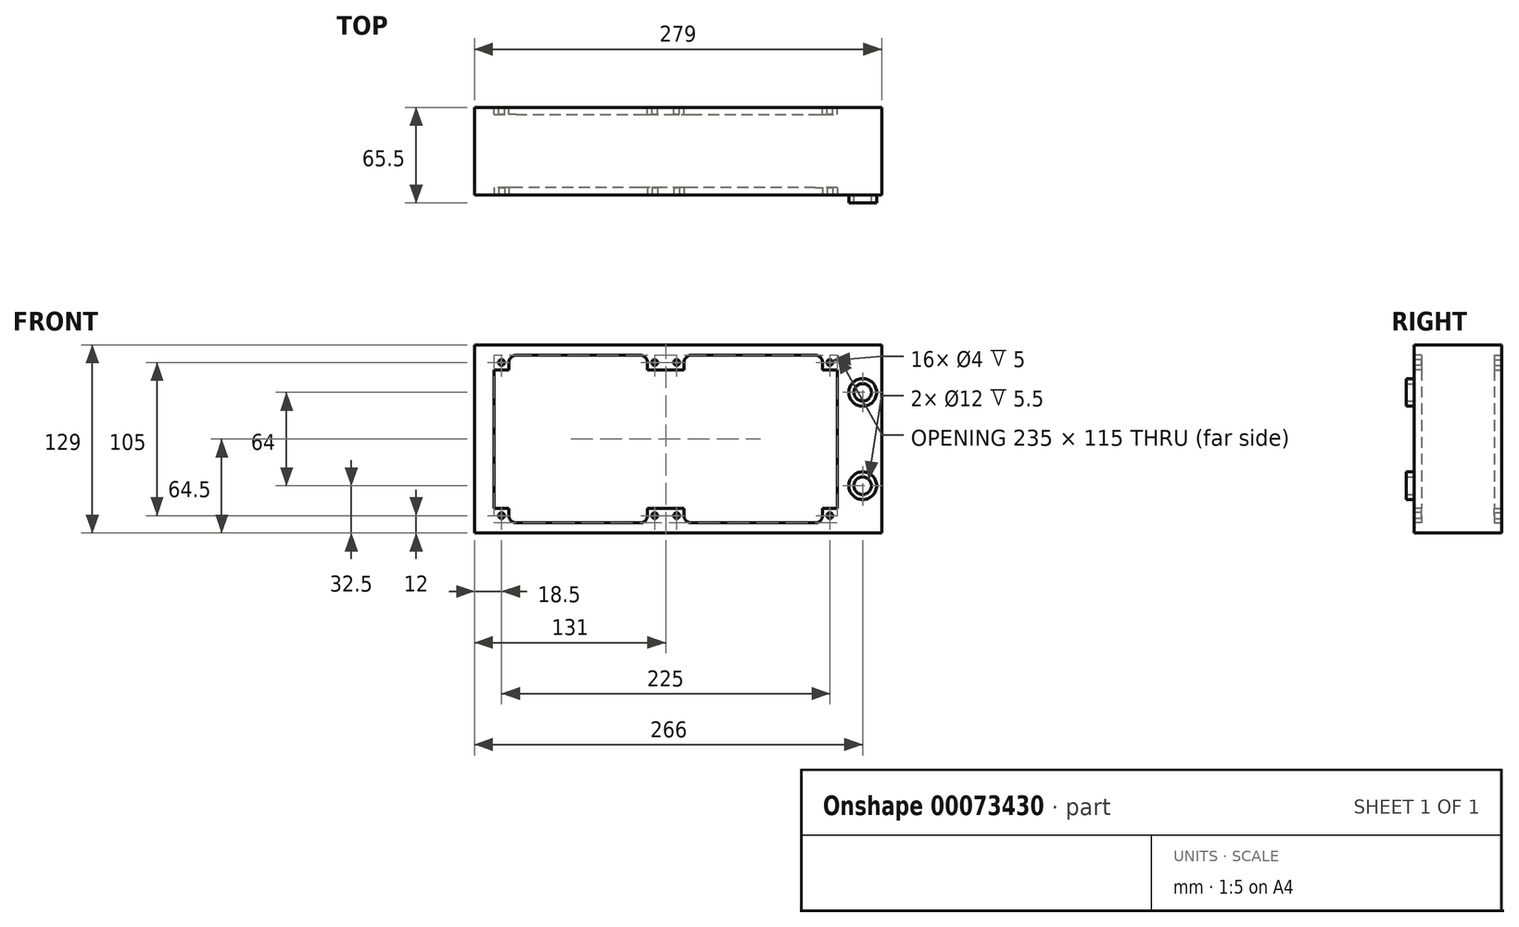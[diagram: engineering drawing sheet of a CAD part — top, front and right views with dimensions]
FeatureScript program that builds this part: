
annotation { "Feature Type Name" : "Feature", "Feature Type Description" : "" }
export const myFeature = defineFeature(function(context is Context, id is Id, definition is map)
    precondition{}
    {
        {
            var Q0;
            Q0=qCreatedBy(makeId("Front.planeOp"),FACE);
            var sketch = newSketch(context, id + "F0", { "sketchPlane" : qUnion([Q0])});
            skLineSegment(sketch, "E0.bottom", {"start": v(0, 64.5) * mm, "end": v(279, 64.5) * mm});
            skLineSegment(sketch, "E0.top", {"start": v(0, -64.5) * mm, "end": v(279, -64.5) * mm});
            skLineSegment(sketch, "E0.left", {"start": v(0, 64.5) * mm, "end": v(0, -64.5) * mm});
            skLineSegment(sketch, "E0.right", {"start": v(279, 64.5) * mm, "end": v(279, -64.5) * mm});
            skSolve(sketch);
        }
        {
            var Q0;
            Q0=qSketchRegion(id+"F0",true);
            extrude(context, id + "F1", {"entities" : qUnion([Q0]), "depth" : 60 * mm});
        }
        {
            var Q0;
            Q0=makeQuery(id+"F1.opExtrude","CAP_FACE",FACE,{"disambiguationData":[OSD([sQuery(id+"F0.wireOp",EDGE,"E0.bottom"),sQuery(id+"F0.wireOp",EDGE,"E0.top"),sQuery(id+"F0.wireOp",EDGE,"E0.left"),sQuery(id+"F0.wireOp",EDGE,"E0.right")])],"isStart":false});
            var sketch = newSketch(context, id + "F2", { "sketchPlane" : qUnion([Q0])});
            skCircle(sketch, "E1", {"center": v(266, -32) * mm, "radius": 9.5 * mm});
            skCircle(sketch, "E2", {"center": v(266, 32) * mm, "radius": 9.5 * mm});
            skLineSegment(sketch, "E3", {"start": v(0, 0) * mm, "end": v(279, 0) * mm, "construction": true});
            skCircle(sketch, "E4", {"center": v(266, 32) * mm, "radius": 6 * mm});
            skCircle(sketch, "E5", {"center": v(266, -32) * mm, "radius": 6 * mm});
            skSolve(sketch);
        }
        {
            var Q0;
            Q0=qSketchRegion(id+"F2",true);
            extrude(context, id + "F3", {"entities" : qUnion([Q0]), "operationType" : NewBodyOperationType.ADD, "depth" : 5.5 * mm});
        }
        {
            var Q0;
            {var subQ0=sQuery(id+"F0.wireOp",EDGE,"E0.right");var subQ1=sQuery(id+"F0.wireOp",EDGE,"E0.left");var subQ2=sQuery(id+"F0.wireOp",EDGE,"E0.top");var subQ3=sQuery(id+"F0.wireOp",EDGE,"E0.bottom");Q0=makeQuery(id+"F3.boolean.opBoolean","SPLIT",FACE,{"disambiguationData":[TD([makeQuery(id+"F1.opExtrude","SWEPT_FACE",FACE,{"disambiguationData":[OSD([subQ3])]})])],"derivedFrom":makeQuery(id+"F1.opExtrude","CAP_FACE",FACE,{"disambiguationData":[OSD([subQ3,subQ2,subQ1,subQ0])],"isStart":false})});}
            var sketch = newSketch(context, id + "F4", { "sketchPlane" : qUnion([Q0])});
            skCircle(sketch, "E6", {"center": v(18.5, 52.5) * mm, "radius": 2 * mm});
            skCircle(sketch, "E7", {"center": v(123.5, 52.5) * mm, "radius": 2 * mm});
            skCircle(sketch, "E8", {"center": v(138.5, 52.5) * mm, "radius": 2 * mm});
            skCircle(sketch, "E9", {"center": v(243.5, 52.5) * mm, "radius": 2 * mm});
            skLineSegment(sketch, "E10", {"start": v(13.5, 47.5) * mm, "end": v(13.5, 0) * mm});
            skLineSegment(sketch, "E11", {"start": v(248.5, 0) * mm, "end": v(248.5, 47.5) * mm});
            skLineSegment(sketch, "E12", {"start": v(248.5, 47.5) * mm, "end": v(238.5, 47.5) * mm});
            skLineSegment(sketch, "E13", {"start": v(238.5, 47.5) * mm, "end": v(238.5, 52.5) * mm});
            skLineSegment(sketch, "E14", {"start": v(233.5, 57.5) * mm, "end": v(148.5, 57.5) * mm});
            skLineSegment(sketch, "E15", {"start": v(143.5, 52.5) * mm, "end": v(143.5, 47.5) * mm});
            skLineSegment(sketch, "E16", {"start": v(143.5, 47.5) * mm, "end": v(118.5, 47.5) * mm});
            skLineSegment(sketch, "E17", {"start": v(118.5, 47.5) * mm, "end": v(118.5, 52.5) * mm});
            skLineSegment(sketch, "E18", {"start": v(113.5, 57.5) * mm, "end": v(28.5, 57.5) * mm});
            skLineSegment(sketch, "E19", {"start": v(23.5, 52.5) * mm, "end": v(23.5, 47.5) * mm});
            skLineSegment(sketch, "E20", {"start": v(23.5, 47.5) * mm, "end": v(13.5, 47.5) * mm});
            skLineSegment(sketch, "E21", {"start": v(0, 0) * mm, "end": v(279, 0) * mm, "construction": true});
            skPoint(sketch, "E22.visualSharp", {"position": v(143.5, 57.5) * mm});
            skArc(sketch, "E22.filletArc", {"start": v(148.5, 57.5) * mm, "mid": v(144.96, 56.04) * mm, "end": v(143.5, 52.5) * mm});
            skPoint(sketch, "E23.visualSharp", {"position": v(118.5, 57.5) * mm});
            skArc(sketch, "E23.filletArc", {"start": v(118.5, 52.5) * mm, "mid": v(117.04, 56.04) * mm, "end": v(113.5, 57.5) * mm});
            skPoint(sketch, "E24.visualSharp", {"position": v(238.5, 57.5) * mm});
            skArc(sketch, "E24.filletArc", {"start": v(238.5, 52.5) * mm, "mid": v(237.04, 56.04) * mm, "end": v(233.5, 57.5) * mm});
            skPoint(sketch, "E25.visualSharp", {"position": v(23.5, 57.5) * mm});
            skArc(sketch, "E25.filletArc", {"start": v(28.5, 57.5) * mm, "mid": v(24.96, 56.04) * mm, "end": v(23.5, 52.5) * mm});
            skCircle(sketch, "E26.MirrorC", {"center": v(243.5, -52.5) * mm, "radius": 2 * mm});
            skLineSegment(sketch, "E27.MirrorCS", {"start": v(248.5, 0) * mm, "end": v(248.5, -47.5) * mm});
            skLineSegment(sketch, "E28.MirrorCS", {"start": v(248.5, -47.5) * mm, "end": v(238.5, -47.5) * mm});
            skLineSegment(sketch, "E29.MirrorCS", {"start": v(238.5, -47.5) * mm, "end": v(238.5, -52.5) * mm});
            skArc(sketch, "E30.MirrorCS", {"start": v(238.5, -52.5) * mm, "mid": v(237.04, -56.04) * mm, "end": v(233.5, -57.5) * mm});
            skLineSegment(sketch, "E31.MirrorCS", {"start": v(233.5, -57.5) * mm, "end": v(148.5, -57.5) * mm});
            skArc(sketch, "E32.MirrorCS", {"start": v(148.5, -57.5) * mm, "mid": v(144.96, -56.04) * mm, "end": v(143.5, -52.5) * mm});
            skLineSegment(sketch, "E33.MirrorCS", {"start": v(143.5, -52.5) * mm, "end": v(143.5, -47.5) * mm});
            skCircle(sketch, "E34.MirrorC", {"center": v(138.5, -52.5) * mm, "radius": 2 * mm});
            skCircle(sketch, "E35.MirrorC", {"center": v(123.5, -52.5) * mm, "radius": 2 * mm});
            skLineSegment(sketch, "E36.MirrorCS", {"start": v(143.5, -47.5) * mm, "end": v(118.5, -47.5) * mm});
            skCircle(sketch, "E37.MirrorC", {"center": v(18.5, -52.5) * mm, "radius": 2 * mm});
            skLineSegment(sketch, "E38.MirrorCS", {"start": v(118.5, -47.5) * mm, "end": v(118.5, -52.5) * mm});
            skArc(sketch, "E39.MirrorCS", {"start": v(118.5, -52.5) * mm, "mid": v(117.04, -56.04) * mm, "end": v(113.5, -57.5) * mm});
            skLineSegment(sketch, "E40.MirrorCS", {"start": v(113.5, -57.5) * mm, "end": v(28.5, -57.5) * mm});
            skArc(sketch, "E41.MirrorCS", {"start": v(28.5, -57.5) * mm, "mid": v(24.96, -56.04) * mm, "end": v(23.5, -52.5) * mm});
            skLineSegment(sketch, "E42.MirrorCS", {"start": v(23.5, -52.5) * mm, "end": v(23.5, -47.5) * mm});
            skLineSegment(sketch, "E43.MirrorCS", {"start": v(13.5, -47.5) * mm, "end": v(13.5, 0) * mm});
            skLineSegment(sketch, "E44.MirrorCS", {"start": v(23.5, -47.5) * mm, "end": v(13.5, -47.5) * mm});
            skSolve(sketch);
        }
        {
            var Q0;
            Q0=qSketchRegion(id+"F4",true);
            extrude(context, id + "F5", {"entities" : qUnion([Q0]), "operationType" : NewBodyOperationType.REMOVE, "oppositeDirection" : true, "depth" : 5 * mm});
        }
        {
            var Q0;
            Q0=makeQuery(id+"F1.opExtrude","CAP_FACE",FACE,{"disambiguationData":[OSD([sQuery(id+"F0.wireOp",EDGE,"E0.bottom"),sQuery(id+"F0.wireOp",EDGE,"E0.top"),sQuery(id+"F0.wireOp",EDGE,"E0.left"),sQuery(id+"F0.wireOp",EDGE,"E0.right")])],"isStart":true});
            var sketch = newSketch(context, id + "F6", { "sketchPlane" : qUnion([Q0])});
            skCircle(sketch, "E45", {"center": v(-243.5, 52.5) * mm, "radius": 2 * mm});
            skCircle(sketch, "E46", {"center": v(-138.5, 52.5) * mm, "radius": 2 * mm});
            skCircle(sketch, "E47", {"center": v(-123.5, 52.5) * mm, "radius": 2 * mm});
            skCircle(sketch, "E48", {"center": v(-18.5, 52.5) * mm, "radius": 2 * mm});
            skLineSegment(sketch, "E49", {"start": v(-248.5, 47.5) * mm, "end": v(-248.5, 0) * mm});
            skLineSegment(sketch, "E50", {"start": v(-13.5, 0) * mm, "end": v(-13.5, 47.5) * mm});
            skLineSegment(sketch, "E51", {"start": v(-13.5, 47.5) * mm, "end": v(-23.5, 47.5) * mm});
            skLineSegment(sketch, "E52", {"start": v(-23.5, 47.5) * mm, "end": v(-23.5, 52.5) * mm});
            skLineSegment(sketch, "E53", {"start": v(-28.5, 57.5) * mm, "end": v(-113.5, 57.5) * mm});
            skLineSegment(sketch, "E54", {"start": v(-118.5, 52.5) * mm, "end": v(-118.5, 47.5) * mm});
            skLineSegment(sketch, "E55", {"start": v(-118.5, 47.5) * mm, "end": v(-143.5, 47.5) * mm});
            skLineSegment(sketch, "E56", {"start": v(-143.5, 47.5) * mm, "end": v(-143.5, 52.5) * mm});
            skLineSegment(sketch, "E57", {"start": v(-148.5, 57.5) * mm, "end": v(-233.5, 57.5) * mm});
            skLineSegment(sketch, "E58", {"start": v(-238.5, 52.5) * mm, "end": v(-238.5, 47.5) * mm});
            skLineSegment(sketch, "E59", {"start": v(-238.5, 47.5) * mm, "end": v(-248.5, 47.5) * mm});
            skLineSegment(sketch, "E60", {"start": v(-279, 0) * mm, "end": v(0, 0) * mm, "construction": true});
            skPoint(sketch, "E61.visualSharp", {"position": v(-118.5, 57.5) * mm});
            skArc(sketch, "E61.filletArc", {"start": v(-113.5, 57.5) * mm, "mid": v(-117.04, 56.04) * mm, "end": v(-118.5, 52.5) * mm});
            skPoint(sketch, "E62.visualSharp", {"position": v(-143.5, 57.5) * mm});
            skArc(sketch, "E62.filletArc", {"start": v(-143.5, 52.5) * mm, "mid": v(-144.96, 56.04) * mm, "end": v(-148.5, 57.5) * mm});
            skPoint(sketch, "E63.visualSharp", {"position": v(-23.5, 57.5) * mm});
            skArc(sketch, "E63.filletArc", {"start": v(-23.5, 52.5) * mm, "mid": v(-24.96, 56.04) * mm, "end": v(-28.5, 57.5) * mm});
            skPoint(sketch, "E64.visualSharp", {"position": v(-238.5, 57.5) * mm});
            skArc(sketch, "E64.filletArc", {"start": v(-233.5, 57.5) * mm, "mid": v(-237.04, 56.04) * mm, "end": v(-238.5, 52.5) * mm});
            skCircle(sketch, "E65.MirrorC", {"center": v(-18.5, -52.5) * mm, "radius": 2 * mm});
            skLineSegment(sketch, "E66.MirrorCS", {"start": v(-13.5, 0) * mm, "end": v(-13.5, -47.5) * mm});
            skLineSegment(sketch, "E67.MirrorCS", {"start": v(-13.5, -47.5) * mm, "end": v(-23.5, -47.5) * mm});
            skLineSegment(sketch, "E68.MirrorCS", {"start": v(-23.5, -47.5) * mm, "end": v(-23.5, -52.5) * mm});
            skArc(sketch, "E69.MirrorCS", {"start": v(-23.5, -52.5) * mm, "mid": v(-24.96, -56.04) * mm, "end": v(-28.5, -57.5) * mm});
            skLineSegment(sketch, "E70.MirrorCS", {"start": v(-28.5, -57.5) * mm, "end": v(-113.5, -57.5) * mm});
            skArc(sketch, "E71.MirrorCS", {"start": v(-113.5, -57.5) * mm, "mid": v(-117.04, -56.04) * mm, "end": v(-118.5, -52.5) * mm});
            skLineSegment(sketch, "E72.MirrorCS", {"start": v(-118.5, -52.5) * mm, "end": v(-118.5, -47.5) * mm});
            skCircle(sketch, "E73.MirrorC", {"center": v(-123.5, -52.5) * mm, "radius": 2 * mm});
            skCircle(sketch, "E74.MirrorC", {"center": v(-138.5, -52.5) * mm, "radius": 2 * mm});
            skLineSegment(sketch, "E75.MirrorCS", {"start": v(-118.5, -47.5) * mm, "end": v(-143.5, -47.5) * mm});
            skCircle(sketch, "E76.MirrorC", {"center": v(-243.5, -52.5) * mm, "radius": 2 * mm});
            skLineSegment(sketch, "E77.MirrorCS", {"start": v(-143.5, -47.5) * mm, "end": v(-143.5, -52.5) * mm});
            skArc(sketch, "E78.MirrorCS", {"start": v(-143.5, -52.5) * mm, "mid": v(-144.96, -56.04) * mm, "end": v(-148.5, -57.5) * mm});
            skLineSegment(sketch, "E79.MirrorCS", {"start": v(-148.5, -57.5) * mm, "end": v(-233.5, -57.5) * mm});
            skArc(sketch, "E80.MirrorCS", {"start": v(-233.5, -57.5) * mm, "mid": v(-237.04, -56.04) * mm, "end": v(-238.5, -52.5) * mm});
            skLineSegment(sketch, "E81.MirrorCS", {"start": v(-238.5, -52.5) * mm, "end": v(-238.5, -47.5) * mm});
            skLineSegment(sketch, "E82.MirrorCS", {"start": v(-248.5, -47.5) * mm, "end": v(-248.5, 0) * mm});
            skLineSegment(sketch, "E83.MirrorCS", {"start": v(-238.5, -47.5) * mm, "end": v(-248.5, -47.5) * mm});
            skSolve(sketch);
        }
        {
            var Q0;
            Q0 = qSketchRegion(id + "F6", true);
            extrude(context, id + "F7", {"entities" : qUnion([Q0]), "operationType" : NewBodyOperationType.REMOVE, "oppositeDirection" : true, "depth" : 5 * mm});
        }
    });
